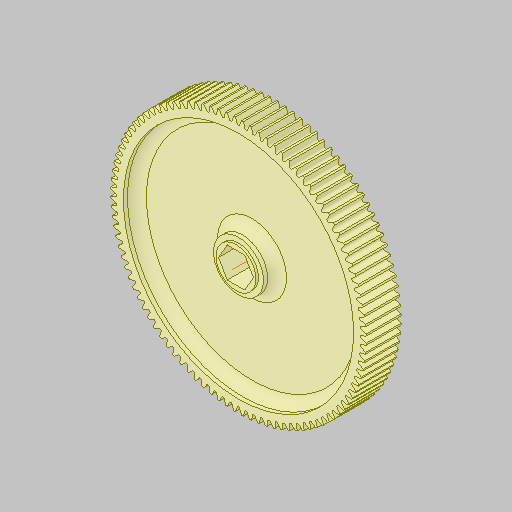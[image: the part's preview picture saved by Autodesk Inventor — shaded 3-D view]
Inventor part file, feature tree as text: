
AUTODESK INVENTOR PART (.ipt)
format: ipt  version: 2023.5 (Build 275446000, 446)  size: 1,011,200 bytes
history: native  units: in
note: dims shown in document units (in); Inventor stores cm internally (conversion verified against a paired STEP export)
features: mirror x1
ambient origin geometry x8: Origin, YZ Plane, XZ Plane, XY Plane, X Axis, Y Axis, Z Axis, Center Point
bodies: Solid1 (feature_tree)
feature tree (1):
  mirror  "Mirror1"
